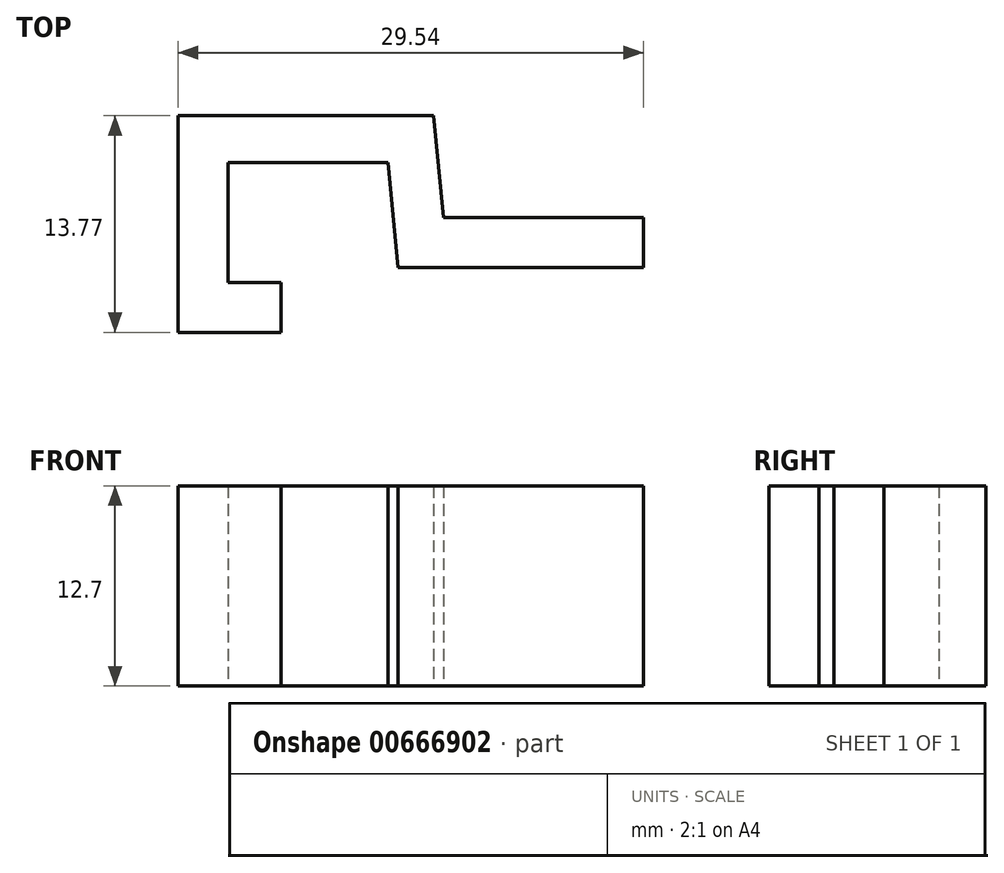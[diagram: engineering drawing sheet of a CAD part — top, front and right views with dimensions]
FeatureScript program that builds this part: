
annotation { "Feature Type Name" : "Feature", "Feature Type Description" : "" }
export const myFeature = defineFeature(function(context is Context, id is Id, definition is map)
    precondition{}
    {
        {
            var Q0;
            Q0=qCreatedBy(makeId("Top.planeOp"),FACE);
            var sketch = newSketch(context, id + "F0", { "sketchPlane" : qUnion([Q0])});
            skLineSegment(sketch, "E0.bottom", {"start": v(-13.34, 2.98) * mm, "end": v(-10.16, 2.98) * mm});
            skLineSegment(sketch, "E0.top", {"start": v(-13.34, -10.8) * mm, "end": v(-10.16, -10.8) * mm});
            skLineSegment(sketch, "E0.left", {"start": v(-13.34, 2.98) * mm, "end": v(-13.34, -10.8) * mm});
            skLineSegment(sketch, "E0.right", {"start": v(-10.16, 2.98) * mm, "end": v(-10.16, -10.8) * mm});
            skLineSegment(sketch, "E1.bottom", {"start": v(-6.79, -7.62) * mm, "end": v(-13.34, -7.62) * mm});
            skLineSegment(sketch, "E1.top", {"start": v(-6.79, -10.8) * mm, "end": v(-13.34, -10.8) * mm});
            skLineSegment(sketch, "E1.left", {"start": v(-6.79, -7.62) * mm, "end": v(-6.79, -10.8) * mm});
            skLineSegment(sketch, "E1.right", {"start": v(-13.34, -7.62) * mm, "end": v(-13.34, -10.8) * mm});
            skLineSegment(sketch, "E2.bottom", {"start": v(-13.34, 2.98) * mm, "end": v(2.9, 2.98) * mm});
            skLineSegment(sketch, "E2.top", {"start": v(-13.34, 0) * mm, "end": v(3.18, 0) * mm});
            skLineSegment(sketch, "E2.left", {"start": v(-13.34, 2.98) * mm, "end": v(-13.34, 0) * mm});
            skLineSegment(sketch, "E2.right", {"start": v(2.9, 2.98) * mm, "end": v(3.18, 0) * mm});
            skLineSegment(sketch, "E3.bottom", {"start": v(1.27, -10.16) * mm, "end": v(4.44, -10.16) * mm});
            skLineSegment(sketch, "E3.top", {"start": v(1.27, -13.34) * mm, "end": v(4.44, -13.34) * mm});
            skLineSegment(sketch, "E3.left", {"start": v(1.27, -10.16) * mm, "end": v(1.27, -13.34) * mm});
            skLineSegment(sketch, "E3.right", {"start": v(4.44, -10.16) * mm, "end": v(4.44, -13.34) * mm});
            skLineSegment(sketch, "E4", {"start": v(0, 0) * mm, "end": v(1.27, -13.34) * mm});
            skLineSegment(sketch, "E5", {"start": v(3.18, 0) * mm, "end": v(4.44, -13.34) * mm});
            skLineSegment(sketch, "E6.left", {"start": v(0, 2.98) * mm, "end": v(0, 0) * mm});
            skPoint(sketch, "E7.oppositeSnap0", {"position": v(3.81, -6.67) * mm});
            skLineSegment(sketch, "E7.bottom", {"start": v(3.5, -3.5) * mm, "end": v(16.2, -3.5) * mm});
            skLineSegment(sketch, "E7.top", {"start": v(3.5, -6.67) * mm, "end": v(16.2, -6.67) * mm});
            skLineSegment(sketch, "E7.left", {"start": v(3.5, -3.5) * mm, "end": v(3.5, -6.67) * mm});
            skLineSegment(sketch, "E7.right", {"start": v(16.2, -3.5) * mm, "end": v(16.2, -6.67) * mm});
            skSolve(sketch);
        }
        {
            var Q0;
            Q0=qSketchRegion(id+"F0",true);
            extrude(context, id + "F1", {"entities" : qUnion([Q0]), "depth" : 12.7 * mm, "offsetDistance" : 25.4 * mm});
        }
        {
            var Q0;
            Q0=qCreatedBy(makeId("Top.planeOp"),FACE);
            var sketch = newSketch(context, id + "F2", { "sketchPlane" : qUnion([Q0])});
            skLineSegment(sketch, "E8.bottom", {"start": v(6.88, -6.67) * mm, "end": v(0, -6.67) * mm});
            skLineSegment(sketch, "E8.top", {"start": v(6.88, -16.42) * mm, "end": v(0, -16.42) * mm});
            skLineSegment(sketch, "E8.left", {"start": v(6.88, -6.67) * mm, "end": v(6.88, -16.42) * mm});
            skLineSegment(sketch, "E8.right", {"start": v(0, -6.67) * mm, "end": v(0, -16.42) * mm});
            skSolve(sketch);
        }
        {
            var Q0;
            Q0=qSketchRegion(id+"F2",true);
            extrude(context, id + "F3", {"entities" : qUnion([Q0]), "operationType" : NewBodyOperationType.REMOVE, "depth" : 25.4 * mm, "offsetDistance" : 25.4 * mm});
        }
    });
